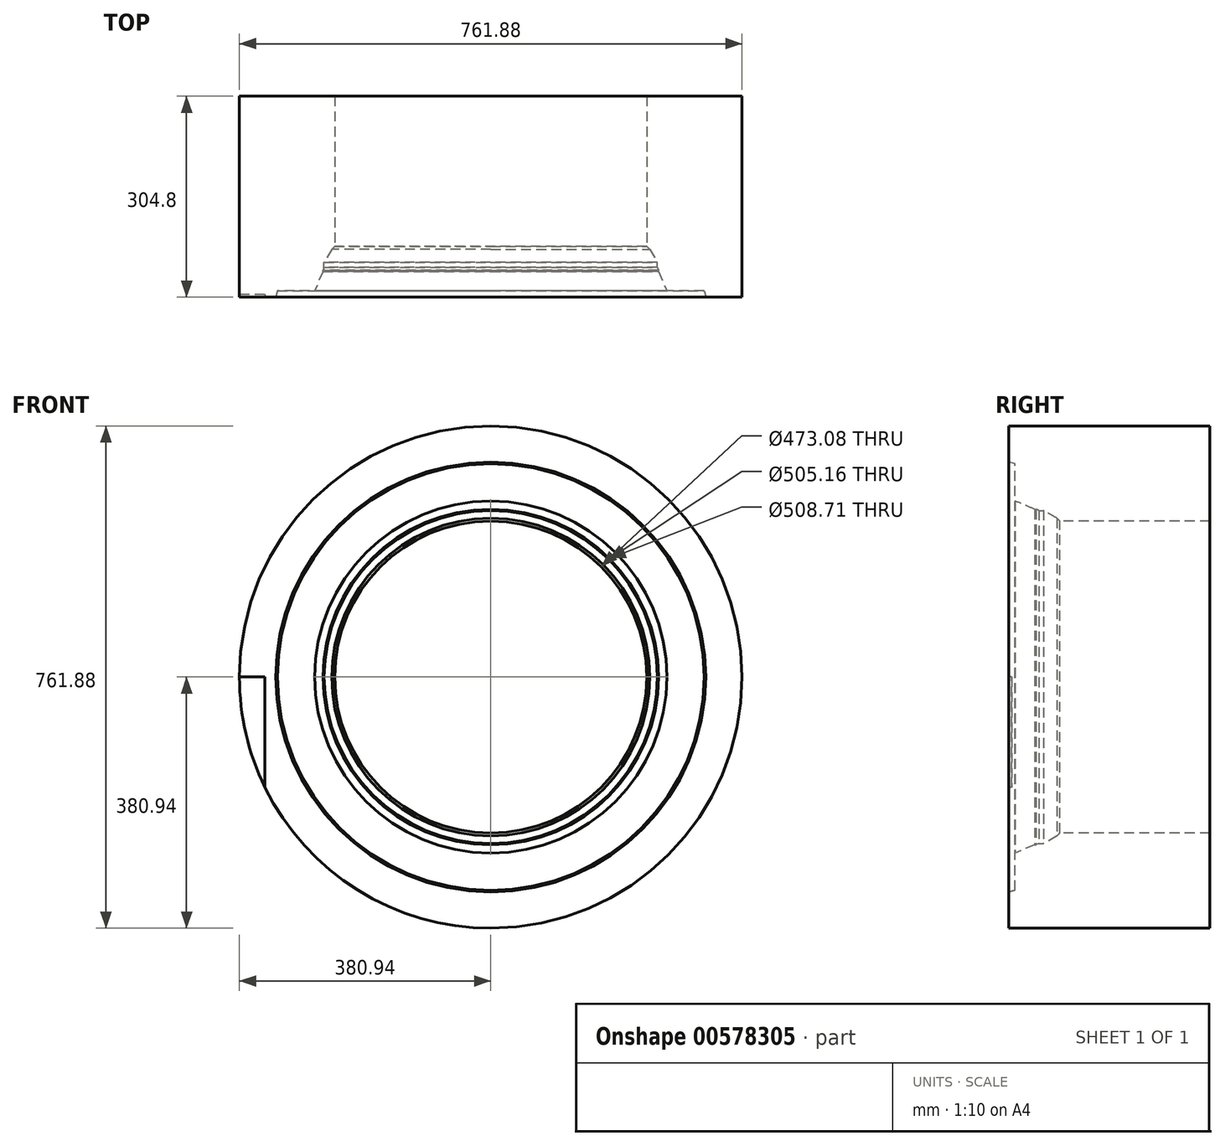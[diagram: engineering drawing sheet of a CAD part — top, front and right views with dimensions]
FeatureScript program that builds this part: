
annotation { "Feature Type Name" : "Feature", "Feature Type Description" : "" }
export const myFeature = defineFeature(function(context is Context, id is Id, definition is map)
    precondition{}
    {
        {
            var Q0;
            Q0=qCreatedBy(makeId("Front.planeOp"),FACE);
            var sketch = newSketch(context, id + "F0", { "sketchPlane" : qUnion([Q0])});
            skCircle(sketch, "E0", {"center": v(0, 0) * mm, "radius": 236.54 * mm});
            skCircle(sketch, "E1", {"center": v(0, 0) * mm, "radius": 380.94 * mm});
            skSolve(sketch);
        }
        {
            var Q0;
            Q0=qSketchRegion(id+"F0",true);
            extrude(context, id + "F1", {"entities" : qUnion([Q0]), "oppositeDirection" : true, "depth" : 304.8 * mm, "offsetDistance" : 25.4 * mm});
        }
        {
            var Q0;
            Q0=qCreatedBy(makeId("Right.planeOp"),FACE);
            var sketch = newSketch(context, id + "F2", { "sketchPlane" : qUnion([Q0])});
            skLineSegment(sketch, "E2", {"start": v(0, 0) * mm, "end": v(-223.81, 0) * mm});
            skPoint(sketch, "E3", {"position": v(0, 325.9) * mm});
            skLineSegment(sketch, "E4", {"start": v(9.52, 323.44) * mm, "end": v(9.53, 0) * mm});
            skLineSegment(sketch, "E5", {"start": v(0, 325.9) * mm, "end": v(9.53, 323.44) * mm});
            skLineSegment(sketch, "E6", {"start": v(0, 0) * mm, "end": v(9.53, 0) * mm});
            skLineSegment(sketch, "E7", {"start": v(0, 325.9) * mm, "end": v(-38.14, 325.9) * mm});
            skLineSegment(sketch, "E8", {"start": v(-38.14, 325.9) * mm, "end": v(0, -5.87) * mm});
            skSolve(sketch);
        }
        {
            var Q0;
            Q0=qSketchRegion(id+"F2",true);
            var Q1;
            Q1=sQuery(id+"F2.wireOp",EDGE,"E2");
            revolve(context, id + "F3", {"operationType" : NewBodyOperationType.REMOVE, "entities" : qUnion([Q0]), "axis" : qUnion([Q1]), "revolveType" : RevolveType.FULL, "oppositeDirection" : true});
        }
        {
            var Q0;
            Q0=qCreatedBy(makeId("Right.planeOp"),FACE);
            var sketch = newSketch(context, id + "F4", { "sketchPlane" : qUnion([Q0])});
            skPoint(sketch, "E9", {"position": v(9.52, 267) * mm});
            skLineSegment(sketch, "E10", {"start": v(9.52, 267) * mm, "end": v(39.3, 254.36) * mm});
            skLineSegment(sketch, "E11", {"start": v(41.25, 254.36) * mm, "end": v(39.3, 254.36) * mm});
            skLineSegment(sketch, "E12", {"start": v(41.25, 254.36) * mm, "end": v(45.44, 252.58) * mm});
            skLineSegment(sketch, "E13", {"start": v(45.44, 252.58) * mm, "end": v(52.7, 252.58) * mm});
            skLineSegment(sketch, "E14", {"start": v(52.7, 252.58) * mm, "end": v(72.8, 240.98) * mm});
            skLineSegment(sketch, "E15", {"start": v(72.8, 240.98) * mm, "end": v(83.79, 229.98) * mm});
            skLineSegment(sketch, "E16", {"start": v(9.52, 267) * mm, "end": v(-83.95, 267) * mm});
            skLineSegment(sketch, "E17", {"start": v(-83.95, 267) * mm, "end": v(-48.08, 188) * mm});
            skLineSegment(sketch, "E18", {"start": v(-48.08, 188) * mm, "end": v(83.79, 229.98) * mm});
            skSolve(sketch);
        }
        {
            var Q0;
            Q0=qSketchRegion(id+"F4",true);
            var Q1;
            Q1=makeQuery(id+"F1.opExtrude","SWEPT_FACE",FACE,{"disambiguationData":[OSD([sQuery(id+"F0.wireOp",EDGE,"E0")])]});
            revolve(context, id + "F5", {"operationType" : NewBodyOperationType.REMOVE, "entities" : qUnion([Q0]), "axis" : qUnion([Q1]), "revolveType" : RevolveType.FULL, "oppositeDirection" : true});
        }
        {
            var Q0;
            Q0=qCreatedBy(makeId("Top.planeOp"),FACE);
            var sketch = newSketch(context, id + "F6", { "sketchPlane" : qUnion([Q0])});
            skLineSegment(sketch, "E19.bottom", {"start": v(-395.47, -13.39) * mm, "end": v(-342.23, -13.39) * mm});
            skLineSegment(sketch, "E19.top", {"start": v(-395.47, 4.5) * mm, "end": v(-342.23, 4.5) * mm});
            skLineSegment(sketch, "E19.left", {"start": v(-395.47, -13.39) * mm, "end": v(-395.47, 4.5) * mm});
            skLineSegment(sketch, "E19.right", {"start": v(-342.23, -13.39) * mm, "end": v(-342.23, 4.5) * mm});
            skSolve(sketch);
        }
        {
            var Q0;
            Q0=qSketchRegion(id+"F6",true);
            extrude(context, id + "F7", {"entities" : qUnion([Q0]), "operationType" : NewBodyOperationType.REMOVE, "oppositeDirection" : true, "depth" : 231.14 * mm, "offsetDistance" : 25.4 * mm});
        }
    });
